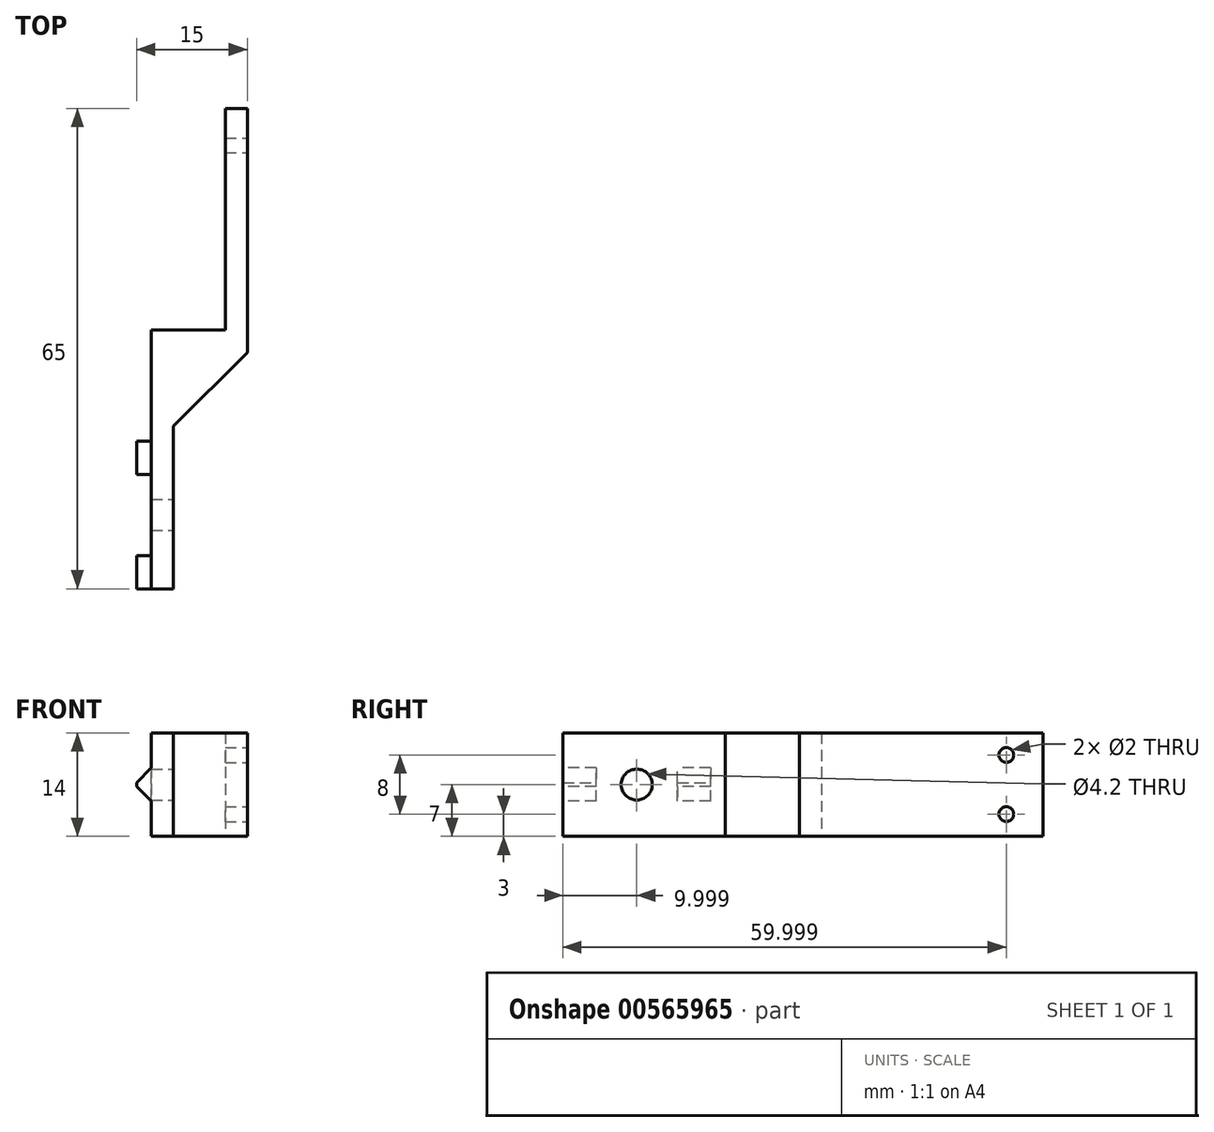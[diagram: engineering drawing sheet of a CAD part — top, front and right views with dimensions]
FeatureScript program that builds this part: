
annotation { "Feature Type Name" : "Feature", "Feature Type Description" : "" }
export const myFeature = defineFeature(function(context is Context, id is Id, definition is map)
    precondition{}
    {
        {
            var Q0;
            Q0=qCreatedBy(makeId("Top.planeOp"),FACE);
            var sketch = newSketch(context, id + "F0", { "sketchPlane" : qUnion([Q0])});
            skLineSegment(sketch, "E0.bottom", {"start": v(-32.57, 52.4) * mm, "end": v(-29.57, 52.4) * mm});
            skLineSegment(sketch, "E0.top", {"start": v(-32.57, 22.4) * mm, "end": v(-29.57, 22.4) * mm});
            skLineSegment(sketch, "E0.left", {"start": v(-32.57, 52.4) * mm, "end": v(-32.57, 22.4) * mm});
            skLineSegment(sketch, "E0.right", {"start": v(-29.57, 52.4) * mm, "end": v(-29.57, 22.4) * mm});
            skLineSegment(sketch, "E1.bottom", {"start": v(-29.57, 22.4) * mm, "end": v(-42.57, 22.4) * mm});
            skLineSegment(sketch, "E1.top", {"start": v(-29.57, 19.4) * mm, "end": v(-42.57, 19.4) * mm});
            skLineSegment(sketch, "E1.left", {"start": v(-29.57, 22.4) * mm, "end": v(-29.57, 19.4) * mm});
            skLineSegment(sketch, "E1.right", {"start": v(-42.57, 22.4) * mm, "end": v(-42.57, 19.4) * mm});
            skLineSegment(sketch, "E2.bottom", {"start": v(-42.57, 19.4) * mm, "end": v(-39.57, 19.4) * mm});
            skLineSegment(sketch, "E2.top", {"start": v(-42.57, -12.6) * mm, "end": v(-39.57, -12.6) * mm});
            skLineSegment(sketch, "E2.left", {"start": v(-42.57, 19.4) * mm, "end": v(-42.57, -12.6) * mm});
            skLineSegment(sketch, "E2.right", {"start": v(-39.57, 19.4) * mm, "end": v(-39.57, -12.6) * mm});
            skSolve(sketch);
        }
        {
            var Q0;
            Q0 = qSketchRegion(id + "F0", true);
            extrude(context, id + "F1", {"entities" : qUnion([Q0]), "depth" : 14 * mm, "offsetDistance" : 25 * mm});
        }
        {
            var Q0;
            Q0=makeQuery(id+"F1.opExtrude","SWEPT_FACE",FACE,{"disambiguationData":[OSD([sQuery(id+"F0.wireOp",EDGE,"E0.right"),sQuery(id+"F0.wireOp",EDGE,"E1.left")])]});
            var sketch = newSketch(context, id + "F2", { "sketchPlane" : qUnion([Q0])});
            skPoint(sketch, "E3", {"position": v(47.4, 11) * mm});
            skPoint(sketch, "E4", {"position": v(47.4, 3) * mm});
            skSolve(sketch);
        }
        {
            var Q0;
            Q0=sQuery(id+"F2.wireOp",VERTEX,"E3");
            var Q1;
            Q1=sQuery(id+"F2.wireOp",VERTEX,"E4");
            var Q2;
            Q2=makeQuery(id+"F1.opExtrude","SWEPT_BODY",BODY,{"disambiguationData":[OSD([sQuery(id+"F0.wireOp",EDGE,"E0.bottom"),sQuery(id+"F0.wireOp",EDGE,"E0.left"),sQuery(id+"F0.wireOp",EDGE,"E0.right"),sQuery(id+"F0.wireOp",EDGE,"E1.bottom"),sQuery(id+"F0.wireOp",EDGE,"E1.top"),sQuery(id+"F0.wireOp",EDGE,"E1.left"),sQuery(id+"F0.wireOp",EDGE,"E1.right"),sQuery(id+"F0.wireOp",EDGE,"E2.top"),sQuery(id+"F0.wireOp",EDGE,"E2.left"),sQuery(id+"F0.wireOp",EDGE,"E2.right")])]});
            hole(context, id + "F3", {"style" : HoleStyle.SIMPLE, "endStyle" : HoleEndStyle.BLIND, "holeDiameter" : 2 * mm, "holeDepth" : 12 * mm, "isTappedThrough" : true, "tappedDepth" : 12 * mm, "tapClearance" : 3, "locations" : qUnion([Q0, Q1]), "scope" : qUnion([Q2])});
        }
        {
            var Q0;
            Q0=makeQuery(id+"F1.opExtrude","SWEPT_FACE",FACE,{"disambiguationData":[OSD([sQuery(id+"F0.wireOp",EDGE,"E1.right"),sQuery(id+"F0.wireOp",EDGE,"E2.left")])]});
            var sketch = newSketch(context, id + "F4", { "sketchPlane" : qUnion([Q0])});
            skPoint(sketch, "E5", {"position": v(2.6, 7) * mm});
            skLineSegment(sketch, "E6.bottom", {"start": v(-7.4, 4.75) * mm, "end": v(-2.9, 4.75) * mm});
            skLineSegment(sketch, "E6.top", {"start": v(-7.4, 9.25) * mm, "end": v(-2.9, 9.25) * mm});
            skLineSegment(sketch, "E6.left", {"start": v(-7.4, 4.75) * mm, "end": v(-7.4, 9.25) * mm});
            skLineSegment(sketch, "E6.right", {"start": v(-2.9, 4.75) * mm, "end": v(-2.9, 9.25) * mm});
            skLineSegment(sketch, "E7.bottom", {"start": v(8.1, 4.75) * mm, "end": v(12.6, 4.75) * mm});
            skLineSegment(sketch, "E7.top", {"start": v(8.1, 9.25) * mm, "end": v(12.6, 9.25) * mm});
            skLineSegment(sketch, "E7.left", {"start": v(8.1, 4.75) * mm, "end": v(8.1, 9.25) * mm});
            skLineSegment(sketch, "E7.right", {"start": v(12.6, 4.75) * mm, "end": v(12.6, 9.25) * mm});
            skSolve(sketch);
        }
        {
            var Q0;
            Q0=makeQuery(id+"F4.imprint","IMPRINT",FACE,{"disambiguationData":[TD([[makeQuery(id+"F4.imprint","IMPRINT",EDGE,{"derivedFrom":sQuery(id+"F4.wireOp",EDGE,"E6.bottom")}),1.0]])]});
            var Q1;
            Q1=makeQuery(id+"F4.imprint","IMPRINT",FACE,{"disambiguationData":[TD([[makeQuery(id+"F4.imprint","IMPRINT",EDGE,{"derivedFrom":sQuery(id+"F4.wireOp",EDGE,"E7.bottom")}),1.0]])]});
            extrude(context, id + "F5", {"entities" : qUnion([Q0, Q1]), "operationType" : NewBodyOperationType.ADD, "depth" : 2 * mm, "offsetDistance" : 25 * mm});
        }
        {
            var Q0;
            Q0=makeQuery(id+"F1.opExtrude","SWEPT_FACE",FACE,{"disambiguationData":[OSD([sQuery(id+"F0.wireOp",EDGE,"E2.right")])]});
            var sketch = newSketch(context, id + "F6", { "sketchPlane" : qUnion([Q0])});
            skPoint(sketch, "E8", {"position": v(-2.6, 7) * mm});
            skSolve(sketch);
        }
        {
            var Q0;
            Q0=sQuery(id+"F6.wireOp",VERTEX,"E8");
            var Q1;
            Q1=makeQuery(id+"F1.opExtrude","SWEPT_BODY",BODY,{"disambiguationData":[OSD([sQuery(id+"F0.wireOp",EDGE,"E0.bottom"),sQuery(id+"F0.wireOp",EDGE,"E0.left"),sQuery(id+"F0.wireOp",EDGE,"E0.right"),sQuery(id+"F0.wireOp",EDGE,"E1.bottom"),sQuery(id+"F0.wireOp",EDGE,"E1.top"),sQuery(id+"F0.wireOp",EDGE,"E1.left"),sQuery(id+"F0.wireOp",EDGE,"E1.right"),sQuery(id+"F0.wireOp",EDGE,"E2.top"),sQuery(id+"F0.wireOp",EDGE,"E2.left"),sQuery(id+"F0.wireOp",EDGE,"E2.right")])]});
            hole(context, id + "F7", {"style" : HoleStyle.SIMPLE, "endStyle" : HoleEndStyle.THROUGH, "holeDiameter" : 4.2 * mm, "isTappedThrough" : true, "tappedDepth" : 12 * mm, "tapClearance" : 3, "locations" : qUnion([Q0]), "scope" : qUnion([Q1])});
        }
        {
            var Q0;
            Q0=makeQuery(id+"F1.opExtrude","SWEPT_EDGE",EDGE,{"disambiguationData":[OSD([sQuery(id+"F0.wireOp",EDGE,"E1.top"),sQuery(id+"F0.wireOp",EDGE,"E2.bottom"),sQuery(id+"F0.wireOp",EDGE,"E2.right")])]});
            chamfer(context, id + "F8", {"entities" : qUnion([Q0]), "width" : 10 * mm, "tangentPropagation" : true});
        }
        {
            var Q0;
            Q0=makeQuery(id+"F5.opExtrude","CAP_EDGE",EDGE,{"disambiguationData":[OSD([sQuery(id+"F4.wireOp",EDGE,"E6.bottom")])],"isStart":false});
            var Q1;
            Q1=makeQuery(id+"F5.opExtrude","CAP_EDGE",EDGE,{"disambiguationData":[OSD([sQuery(id+"F4.wireOp",EDGE,"E7.bottom")])],"isStart":false});
            var Q2;
            Q2=makeQuery(id+"F5.opExtrude","CAP_EDGE",EDGE,{"disambiguationData":[OSD([sQuery(id+"F4.wireOp",EDGE,"E7.top")])],"isStart":false});
            var Q3;
            Q3=makeQuery(id+"F5.opExtrude","CAP_EDGE",EDGE,{"disambiguationData":[OSD([sQuery(id+"F4.wireOp",EDGE,"E6.top")])],"isStart":false});
            chamfer(context, id + "F9", {"entities" : qUnion([Q0, Q1, Q2, Q3]), "width" : 2 * mm, "tangentPropagation" : true});
        }
    });
